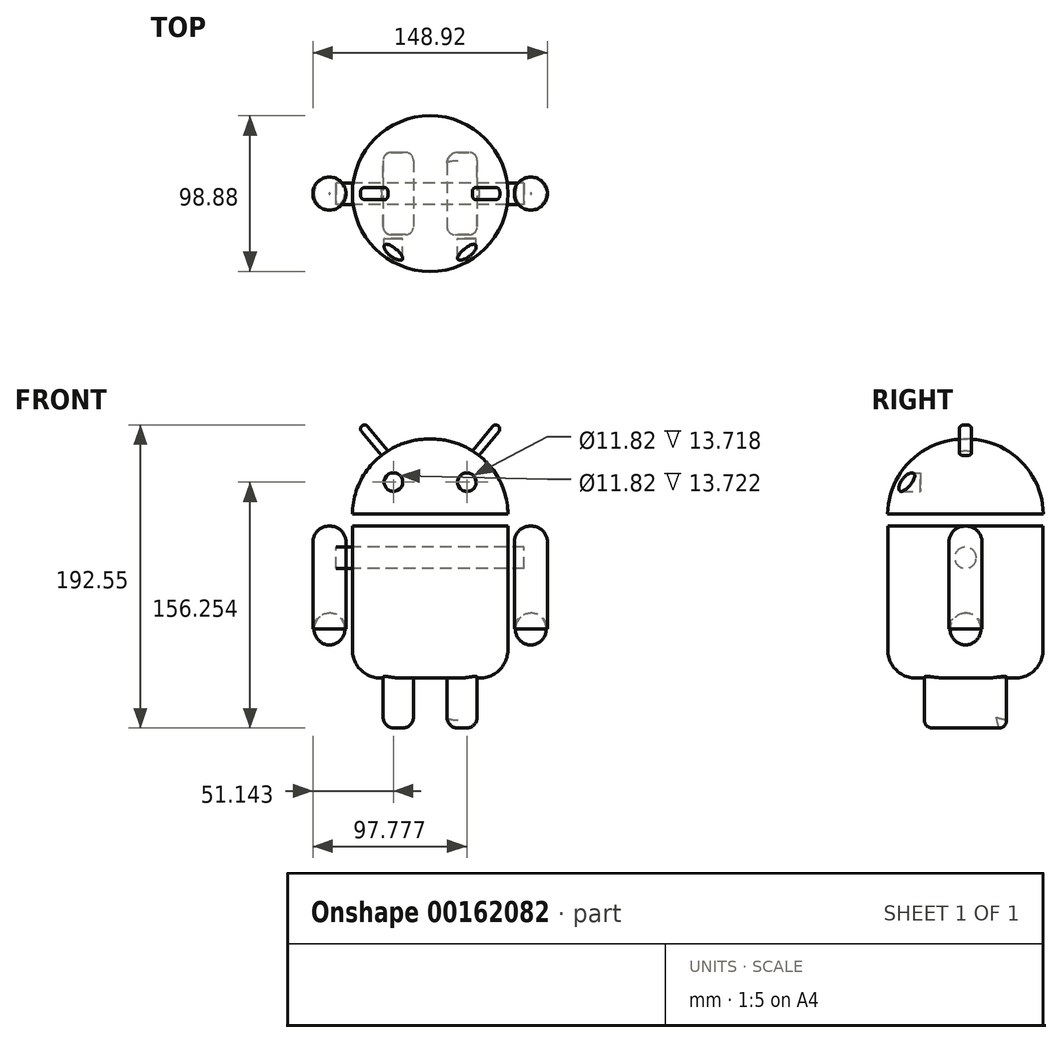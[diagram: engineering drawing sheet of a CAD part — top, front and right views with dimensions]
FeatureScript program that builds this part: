
annotation { "Feature Type Name" : "Feature", "Feature Type Description" : "" }
export const myFeature = defineFeature(function(context is Context, id is Id, definition is map)
    precondition{}
    {
        {
            var Q0;
            Q0=qCreatedBy(makeId("Top.planeOp"),FACE);
            var sketch = newSketch(context, id + "F0", { "sketchPlane" : qUnion([Q0])});
            skCircle(sketch, "E0", {"center": v(0, 0) * mm, "radius": 49.33 * mm});
            skSolve(sketch);
        }
        {
            var Q0;
            Q0 = qSketchRegion(id + "F0", true);
            extrude(context, id + "F1", {"entities" : qUnion([Q0]), "depth" : 61.6 * mm, "hasSecondDirection" : true, "secondDirectionOppositeDirection" : true, "secondDirectionDepth" : 34.92 * mm});
        }
        {
            var Q0;
            Q0=makeQuery(id+"F1.opExtrude","CAP_FACE",FACE,{"disambiguationData":[OSD([sQuery(id+"F0.wireOp",EDGE,"E0")])],"isStart":false});
            var sketch = newSketch(context, id + "F2", { "sketchPlane" : qUnion([Q0])});
            skCircle(sketch, "E1", {"center": v(0, 0) * mm, "radius": 42.1 * mm});
            skSolve(sketch);
        }
        {
            var Q0;
            Q0=sQuery(id+"F2.wireOp",EDGE,"E1");
            extrude(context, id + "F3", {"bodyType" : ToolBodyType.SURFACE, "surfaceEntities" : qUnion([Q0]), "depth" : 7.62 * mm});
        }
        {
            var Q0;
            Q0=makeQuery(id+"F1.opExtrude","CAP_FACE",FACE,{"disambiguationData":[OSD([sQuery(id+"F0.wireOp",EDGE,"E0")])],"isStart":false});
            var sketch = newSketch(context, id + "F4", { "sketchPlane" : qUnion([Q0])});
            skCircle(sketch, "E2", {"center": v(0, 0) * mm, "radius": 49.44 * mm});
            skSolve(sketch);
        }
        {
            var Q0;
            Q0 = qSketchRegion(id + "F4", true);
            extrude(context, id + "F5", {"entities" : qUnion([Q0]), "depth" : 55.24 * mm, "hasSecondDirection" : true, "secondDirectionOppositeDirection" : false, "secondDirectionDepth" : 7.62 * mm});
        }
        {
            var Q0;
            Q0=makeQuery(id+"F5.opExtrude","CAP_EDGE",EDGE,{"disambiguationData":[OSD([sQuery(id+"F4.wireOp",EDGE,"E2")])],"isStart":false});
            fillet(context, id + "F6", {"entities" : qUnion([Q0]), "radius" : 48.26 * mm, "tangentPropagation" : true, "allowEdgeOverflow" : false});
        }
        {
            var Q0;
            Q0=makeQuery(id+"F1.opExtrude","CAP_EDGE",EDGE,{"disambiguationData":[OSD([sQuery(id+"F0.wireOp",EDGE,"E0")])],"isStart":true});
            fillet(context, id + "F7", {"entities" : qUnion([Q0]), "radius" : 17.78 * mm, "tangentPropagation" : true, "allowEdgeOverflow" : false});
        }
        {
            var Q0;
            Q0=qCreatedBy(makeId("Top.planeOp"),FACE);
            var sketch = newSketch(context, id + "F8", { "sketchPlane" : qUnion([Q0])});
            skCircle(sketch, "E3", {"center": v(-63.94, 0) * mm, "radius": 10.52 * mm});
            skCircle(sketch, "E4.MirrorC", {"center": v(63.94, 0) * mm, "radius": 10.52 * mm});
            skSolve(sketch);
        }
        {
            var Q0;
            Q0 = qSketchRegion(id + "F8", true);
            extrude(context, id + "F9", {"entities" : qUnion([Q0]), "depth" : 61.6 * mm, "hasSecondDirection" : true, "secondDirectionOppositeDirection" : true, "secondDirectionDepth" : 13.97 * mm});
        }
        {
            var Q0;
            Q0=makeQuery(id+"F9.opExtrude","CAP_EDGE",EDGE,{"disambiguationData":[OSD([sQuery(id+"F8.wireOp",EDGE,"E3")])],"isStart":false});
            var Q1;
            Q1=makeQuery(id+"F9.opExtrude","CAP_EDGE",EDGE,{"disambiguationData":[OSD([sQuery(id+"F8.wireOp",EDGE,"E3")])],"isStart":true});
            var Q2;
            Q2=makeQuery(id+"F9.opExtrude","CAP_EDGE",EDGE,{"disambiguationData":[OSD([sQuery(id+"F8.wireOp",EDGE,"E4.MirrorC")])],"isStart":false});
            var Q3;
            Q3=makeQuery(id+"F9.opExtrude","CAP_EDGE",EDGE,{"disambiguationData":[OSD([sQuery(id+"F8.wireOp",EDGE,"E4.MirrorC")])],"isStart":true});
            fillet(context, id + "F10", {"entities" : qUnion([Q0, Q1, Q2, Q3]), "radius" : 10.16 * mm, "tangentPropagation" : true, "allowEdgeOverflow" : false});
        }
        {
            var Q0;
            Q0=qCreatedBy(makeId("Right.planeOp"),FACE);
            var sketch = newSketch(context, id + "F11", { "sketchPlane" : qUnion([Q0])});
            skCircle(sketch, "E5", {"center": v(0, 41.46) * mm, "radius": 6.83 * mm});
            skSolve(sketch);
        }
        {
            var Q0;
            Q0 = qSketchRegion(id + "F11", true);
            extrude(context, id + "F12", {"entities" : qUnion([Q0]), "endBound" : BoundingType.SYMMETRIC, "depth" : 119.38 * mm});
        }
        {
            var Q0;
            Q0=qCreatedBy(makeId("Top.planeOp"),FACE);
            var sketch = newSketch(context, id + "F13", { "sketchPlane" : qUnion([Q0])});
            skLineSegment(sketch, "E6.bottom", {"start": v(-10.67, 26.14) * mm, "end": v(-29.84, 26.14) * mm});
            skLineSegment(sketch, "E6.top", {"start": v(-10.67, -26.14) * mm, "end": v(-29.84, -26.14) * mm});
            skLineSegment(sketch, "E6.left", {"start": v(-10.67, 26.14) * mm, "end": v(-10.67, -26.14) * mm});
            skLineSegment(sketch, "E6.right", {"start": v(-29.84, 26.14) * mm, "end": v(-29.84, -26.14) * mm});
            skPoint(sketch, "E6.middle", {"position": v(-20.26, 0) * mm});
            skLineSegment(sketch, "E7.MirrorCS", {"start": v(10.67, 26.14) * mm, "end": v(10.67, -26.14) * mm});
            skLineSegment(sketch, "E8.MirrorCS", {"start": v(10.67, -26.14) * mm, "end": v(29.84, -26.14) * mm});
            skLineSegment(sketch, "E9.MirrorCS", {"start": v(29.84, 26.14) * mm, "end": v(29.84, -26.14) * mm});
            skLineSegment(sketch, "E10.MirrorCS", {"start": v(10.67, 26.14) * mm, "end": v(29.84, 26.14) * mm});
            skSolve(sketch);
        }
        {
            var Q0;
            Q0 = qSketchRegion(id + "F13", true);
            extrude(context, id + "F14", {"entities" : qUnion([Q0]), "operationType" : NewBodyOperationType.ADD, "oppositeDirection" : true, "depth" : 66.67 * mm});
        }
        {
            var Q0;
            Q0=makeQuery(id+"F14.opExtrude","SWEPT_EDGE",EDGE,{"disambiguationData":[OSD([sQuery(id+"F13.wireOp",EDGE,"E6.top"),sQuery(id+"F13.wireOp",EDGE,"E6.right")])]});
            var Q1;
            Q1=makeQuery(id+"F14.opExtrude","CAP_EDGE",EDGE,{"disambiguationData":[OSD([sQuery(id+"F13.wireOp",EDGE,"E6.top")])],"isStart":false});
            var Q2;
            Q2=makeQuery(id+"F14.opExtrude","SWEPT_EDGE",EDGE,{"disambiguationData":[OSD([sQuery(id+"F13.wireOp",EDGE,"E6.top"),sQuery(id+"F13.wireOp",EDGE,"E6.left")])]});
            var Q3;
            Q3=makeQuery(id+"F14.opExtrude","SWEPT_EDGE",EDGE,{"disambiguationData":[OSD([sQuery(id+"F13.wireOp",EDGE,"E7.MirrorCS"),sQuery(id+"F13.wireOp",EDGE,"E8.MirrorCS")])]});
            var Q4;
            Q4=makeQuery(id+"F14.opExtrude","SWEPT_EDGE",EDGE,{"disambiguationData":[OSD([sQuery(id+"F13.wireOp",EDGE,"E8.MirrorCS"),sQuery(id+"F13.wireOp",EDGE,"E9.MirrorCS")])]});
            var Q5;
            Q5=makeQuery(id+"F14.opExtrude","CAP_EDGE",EDGE,{"disambiguationData":[OSD([sQuery(id+"F13.wireOp",EDGE,"E8.MirrorCS")])],"isStart":false});
            var Q6;
            Q6=makeQuery(id+"F14.opExtrude","SWEPT_EDGE",EDGE,{"disambiguationData":[OSD([sQuery(id+"F13.wireOp",EDGE,"E9.MirrorCS"),sQuery(id+"F13.wireOp",EDGE,"E10.MirrorCS")])]});
            var Q7;
            Q7=makeQuery(id+"F14.opExtrude","CAP_EDGE",EDGE,{"disambiguationData":[OSD([sQuery(id+"F13.wireOp",EDGE,"E10.MirrorCS")])],"isStart":false});
            var Q8;
            Q8=makeQuery(id+"F14.opExtrude","SWEPT_EDGE",EDGE,{"disambiguationData":[OSD([sQuery(id+"F13.wireOp",EDGE,"E6.bottom"),sQuery(id+"F13.wireOp",EDGE,"E6.right")])]});
            var Q9;
            Q9=makeQuery(id+"F14.opExtrude","SWEPT_EDGE",EDGE,{"disambiguationData":[OSD([sQuery(id+"F13.wireOp",EDGE,"E6.bottom"),sQuery(id+"F13.wireOp",EDGE,"E6.left")])]});
            var Q10;
            Q10=makeQuery(id+"F14.opExtrude","CAP_EDGE",EDGE,{"disambiguationData":[OSD([sQuery(id+"F13.wireOp",EDGE,"E6.bottom")])],"isStart":false});
            fillet(context, id + "F15", {"entities" : qUnion([Q0, Q1, Q2, Q3, Q4, Q5, Q6, Q7, Q8, Q9, Q10]), "radius" : 5.08 * mm, "tangentPropagation" : true, "allowEdgeOverflow" : false});
        }
        {
            var Q0;
            Q0=makeQuery(id+"F14.opExtrude","CAP_EDGE",EDGE,{"disambiguationData":[OSD([sQuery(id+"F13.wireOp",EDGE,"E6.right")])],"isStart":false});
            var Q1;
            Q1=makeQuery(id+"F14.opExtrude","CAP_EDGE",EDGE,{"disambiguationData":[OSD([sQuery(id+"F13.wireOp",EDGE,"E6.left")])],"isStart":false});
            var Q2;
            Q2=makeQuery(id+"F14.opExtrude","CAP_EDGE",EDGE,{"disambiguationData":[OSD([sQuery(id+"F13.wireOp",EDGE,"E7.MirrorCS")])],"isStart":false});
            var Q3;
            Q3=makeQuery(id+"F14.opExtrude","CAP_EDGE",EDGE,{"disambiguationData":[OSD([sQuery(id+"F13.wireOp",EDGE,"E9.MirrorCS")])],"isStart":false});
            fillet(context, id + "F16", {"entities" : qUnion([Q0, Q1, Q2, Q3]), "radius" : 6.86 * mm, "tangentPropagation" : true, "allowEdgeOverflow" : false});
        }
        {
            var Q0;
            Q0=qCreatedBy(makeId("Front.planeOp"),FACE);
            var sketch = newSketch(context, id + "F17", { "sketchPlane" : qUnion([Q0])});
            skCircle(sketch, "E11", {"center": v(-23.32, 89.57) * mm, "radius": 5.91 * mm});
            skCircle(sketch, "E12.MirrorC", {"center": v(23.32, 89.57) * mm, "radius": 5.91 * mm});
            skSolve(sketch);
        }
        {
            var Q0;
            Q0 = qSketchRegion(id + "F17", true);
            extrude(context, id + "F18", {"entities" : qUnion([Q0]), "operationType" : NewBodyOperationType.REMOVE, "depth" : 61.6 * mm, "hasSecondDirection" : true, "secondDirectionOppositeDirection" : false, "secondDirectionDepth" : 28.57 * mm});
        }
        {
            var Q0;
            Q0=qCreatedBy(makeId("Front.planeOp"),FACE);
            var sketch = newSketch(context, id + "F19", { "sketchPlane" : qUnion([Q0])});
            skLineSegment(sketch, "E13", {"start": v(-25.65, 104.03) * mm, "end": v(-41.66, 123.33) * mm});
            skArc(sketch, "E14.0.startCap", {"start": v(-23.7, 105.65) * mm, "mid": v(-24.03, 102.07) * mm, "end": v(-27.6, 102.4) * mm});
            skArc(sketch, "E14.0.endCap", {"start": v(-43.62, 121.71) * mm, "mid": v(-43.29, 125.29) * mm, "end": v(-39.7, 124.96) * mm});
            skLineSegment(sketch, "E14.0.left", {"start": v(-27.6, 102.4) * mm, "end": v(-43.62, 121.71) * mm});
            skLineSegment(sketch, "E14.0.right", {"start": v(-23.7, 105.65) * mm, "end": v(-39.7, 124.96) * mm});
            skLineSegment(sketch, "E15.MirrorCS", {"start": v(23.7, 105.65) * mm, "end": v(39.7, 124.96) * mm});
            skArc(sketch, "E16.MirrorCS", {"start": v(43.62, 121.71) * mm, "mid": v(43.29, 125.29) * mm, "end": v(39.7, 124.96) * mm});
            skLineSegment(sketch, "E17.MirrorCS", {"start": v(27.6, 102.4) * mm, "end": v(43.62, 121.71) * mm});
            skArc(sketch, "E18.MirrorCS", {"start": v(23.7, 105.65) * mm, "mid": v(24.03, 102.07) * mm, "end": v(27.6, 102.4) * mm});
            skSolve(sketch);
        }
        {
            var Q0;
            Q0 = qSketchRegion(id + "F19", true);
            extrude(context, id + "F20", {"entities" : qUnion([Q0]), "operationType" : NewBodyOperationType.ADD, "endBound" : BoundingType.SYMMETRIC, "depth" : 7.62 * mm});
        }
        {
            var Q0;
            Q0=makeQuery(id+"F20.opExtrude","CAP_EDGE",EDGE,{"disambiguationData":[OSD([sQuery(id+"F19.wireOp",EDGE,"E14.0.right")])],"isStart":false});
            var Q1;
            Q1=makeQuery(id+"F20.opExtrude","CAP_EDGE",EDGE,{"disambiguationData":[OSD([sQuery(id+"F19.wireOp",EDGE,"E14.0.endCap")])],"isStart":false});
            var Q2;
            Q2=makeQuery(id+"F20.opExtrude","CAP_EDGE",EDGE,{"disambiguationData":[OSD([sQuery(id+"F19.wireOp",EDGE,"E14.0.left")])],"isStart":false});
            var Q3;
            Q3=makeQuery(id+"F20.opExtrude","CAP_EDGE",EDGE,{"disambiguationData":[OSD([sQuery(id+"F19.wireOp",EDGE,"E15.MirrorCS")])],"isStart":false});
            var Q4;
            Q4=makeQuery(id+"F20.opExtrude","CAP_EDGE",EDGE,{"disambiguationData":[OSD([sQuery(id+"F19.wireOp",EDGE,"E16.MirrorCS")])],"isStart":false});
            var Q5;
            Q5=makeQuery(id+"F20.opExtrude","CAP_EDGE",EDGE,{"disambiguationData":[OSD([sQuery(id+"F19.wireOp",EDGE,"E17.MirrorCS")])],"isStart":false});
            var Q6;
            Q6=makeQuery(id+"F20.opExtrude","CAP_EDGE",EDGE,{"disambiguationData":[OSD([sQuery(id+"F19.wireOp",EDGE,"E14.0.left")])],"isStart":true});
            var Q7;
            Q7=makeQuery(id+"F20.opExtrude","CAP_EDGE",EDGE,{"disambiguationData":[OSD([sQuery(id+"F19.wireOp",EDGE,"E14.0.endCap")])],"isStart":true});
            var Q8;
            Q8=makeQuery(id+"F20.opExtrude","CAP_EDGE",EDGE,{"disambiguationData":[OSD([sQuery(id+"F19.wireOp",EDGE,"E14.0.right")])],"isStart":true});
            var Q9;
            Q9=makeQuery(id+"F20.opExtrude","CAP_EDGE",EDGE,{"disambiguationData":[OSD([sQuery(id+"F19.wireOp",EDGE,"E15.MirrorCS")])],"isStart":true});
            var Q10;
            Q10=makeQuery(id+"F20.opExtrude","CAP_EDGE",EDGE,{"disambiguationData":[OSD([sQuery(id+"F19.wireOp",EDGE,"E16.MirrorCS")])],"isStart":true});
            fillet(context, id + "F21", {"entities" : qUnion([Q0, Q1, Q2, Q3, Q4, Q5, Q6, Q7, Q8, Q9, Q10]), "radius" : 2.54 * mm, "tangentPropagation" : true, "allowEdgeOverflow" : false});
        }
    });
